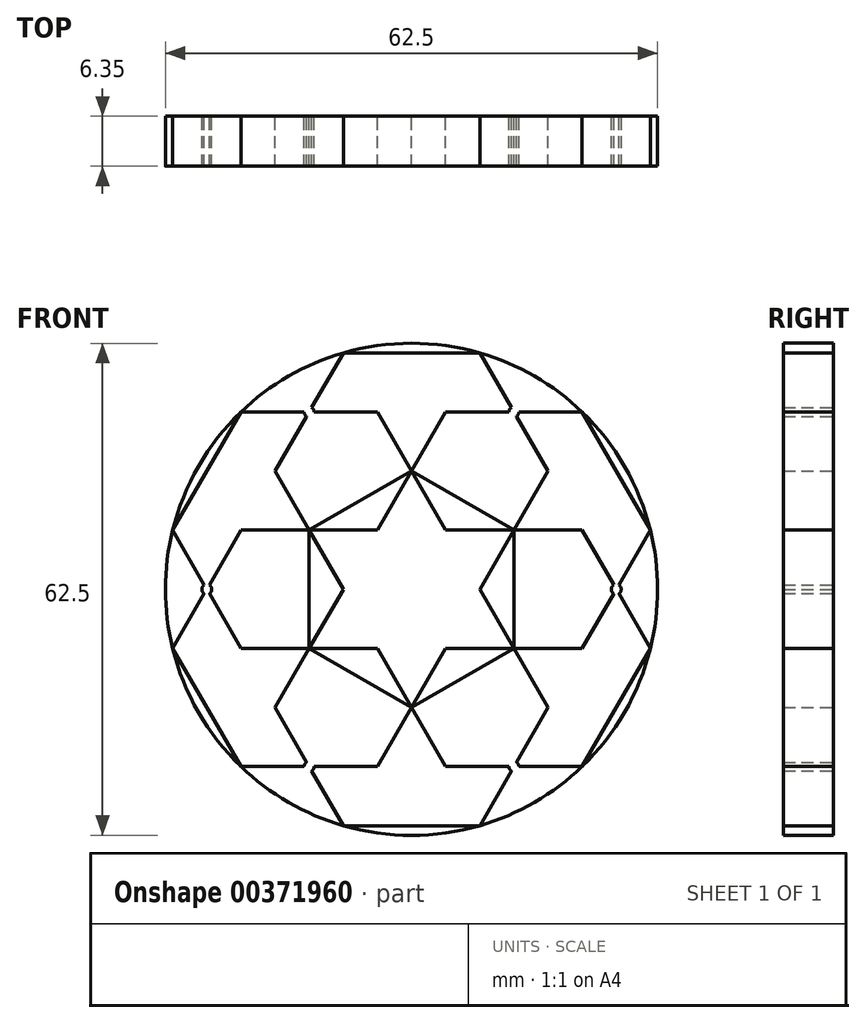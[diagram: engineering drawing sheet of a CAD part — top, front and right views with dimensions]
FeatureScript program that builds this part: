
annotation { "Feature Type Name" : "Feature", "Feature Type Description" : "" }
export const myFeature = defineFeature(function(context is Context, id is Id, definition is map)
    precondition{}
    {
        {
            var Q0;
            Q0=qCreatedBy(makeId("Front.planeOp"),FACE);
            var sketch = newSketch(context, id + "F0", { "sketchPlane" : qUnion([Q0])});
            skLineSegment(sketch, "E0.0", {"start": v(13, 7.5) * mm, "end": v(13, -7.5) * mm});
            skLineSegment(sketch, "E0.1", {"start": v(13, -7.5) * mm, "end": v(0, -15.01) * mm});
            skLineSegment(sketch, "E0.2", {"start": v(0, -15.01) * mm, "end": v(-13, -7.5) * mm});
            skLineSegment(sketch, "E0.3", {"start": v(-13, -7.5) * mm, "end": v(-13, 7.5) * mm});
            skLineSegment(sketch, "E0.4", {"start": v(-13, 7.5) * mm, "end": v(0, 15.01) * mm});
            skLineSegment(sketch, "E0.5", {"start": v(0, 15.01) * mm, "end": v(13, 7.5) * mm});
            skPoint(sketch, "E0.0.midPoint", {"position": v(13, 0) * mm});
            skLineSegment(sketch, "E1.0", {"start": v(17.34, 15.01) * mm, "end": v(8.67, 0) * mm});
            skLineSegment(sketch, "E1.1", {"start": v(8.67, 0) * mm, "end": v(-8.67, 0) * mm});
            skLineSegment(sketch, "E1.2", {"start": v(-8.67, 0) * mm, "end": v(-17.34, 15.01) * mm});
            skLineSegment(sketch, "E1.3", {"start": v(-17.34, 15.01) * mm, "end": v(-13.32, 21.97) * mm});
            skLineSegment(sketch, "E1.4", {"start": v(-8.67, 30.03) * mm, "end": v(8.67, 30.03) * mm});
            skLineSegment(sketch, "E1.5", {"start": v(8.67, 30.03) * mm, "end": v(12.69, 23.07) * mm});
            skPoint(sketch, "E1.0.midPoint", {"position": v(13, 7.5) * mm});
            skLineSegment(sketch, "E2.0", {"start": v(8.67, 0) * mm, "end": v(17.34, -15.01) * mm});
            skLineSegment(sketch, "E2.1", {"start": v(17.34, -15.01) * mm, "end": v(13.32, -21.97) * mm});
            skLineSegment(sketch, "E2.2", {"start": v(8.67, -30.03) * mm, "end": v(-8.67, -30.03) * mm});
            skLineSegment(sketch, "E2.3", {"start": v(-8.67, -30.03) * mm, "end": v(-12.69, -23.07) * mm});
            skLineSegment(sketch, "E2.4", {"start": v(-17.34, -15.01) * mm, "end": v(-8.67, 0) * mm});
            skLineSegment(sketch, "E2.5", {"start": v(-8.67, 0) * mm, "end": v(8.67, 0) * mm});
            skPoint(sketch, "E2.0.midPoint", {"position": v(13, -7.5) * mm});
            skLineSegment(sketch, "E3.0", {"start": v(4.33, 7.5) * mm, "end": v(21.67, 7.5) * mm});
            skLineSegment(sketch, "E3.1", {"start": v(21.67, 7.5) * mm, "end": v(25.69, 0.55) * mm});
            skLineSegment(sketch, "E3.2", {"start": v(30.34, -7.5) * mm, "end": v(21.67, -22.52) * mm});
            skLineSegment(sketch, "E3.3", {"start": v(21.67, -22.52) * mm, "end": v(13.64, -22.52) * mm});
            skLineSegment(sketch, "E3.4", {"start": v(4.33, -22.52) * mm, "end": v(-4.33, -7.5) * mm});
            skLineSegment(sketch, "E3.5", {"start": v(-4.33, -7.5) * mm, "end": v(4.33, 7.5) * mm});
            skLineSegment(sketch, "E4.0", {"start": v(-4.33, -7.5) * mm, "end": v(-21.67, -7.5) * mm});
            skLineSegment(sketch, "E4.1", {"start": v(-21.67, -7.5) * mm, "end": v(-25.69, -0.55) * mm});
            skLineSegment(sketch, "E4.2", {"start": v(-30.34, 7.5) * mm, "end": v(-21.67, 22.52) * mm});
            skLineSegment(sketch, "E4.3", {"start": v(-21.67, 22.52) * mm, "end": v(-13.64, 22.52) * mm});
            skLineSegment(sketch, "E4.4", {"start": v(-4.33, 22.52) * mm, "end": v(4.33, 7.5) * mm});
            skLineSegment(sketch, "E4.5", {"start": v(4.33, 7.5) * mm, "end": v(-4.33, -7.5) * mm});
            skPoint(sketch, "E4.0.midPoint", {"position": v(-13, -7.5) * mm});
            skLineSegment(sketch, "E5.0", {"start": v(4.33, -7.5) * mm, "end": v(-4.33, -22.52) * mm});
            skLineSegment(sketch, "E5.1", {"start": v(-4.33, -22.52) * mm, "end": v(-12.37, -22.52) * mm});
            skLineSegment(sketch, "E5.2", {"start": v(-21.67, -22.52) * mm, "end": v(-30.34, -7.5) * mm});
            skLineSegment(sketch, "E5.3", {"start": v(-30.34, -7.5) * mm, "end": v(-26.32, -0.55) * mm});
            skLineSegment(sketch, "E5.4", {"start": v(-21.67, 7.5) * mm, "end": v(-4.33, 7.5) * mm});
            skLineSegment(sketch, "E5.5", {"start": v(-4.33, 7.5) * mm, "end": v(4.33, -7.5) * mm});
            skPoint(sketch, "E5.0.midPoint", {"position": v(0, -15.01) * mm});
            skLineSegment(sketch, "E6.0", {"start": v(-4.33, 7.5) * mm, "end": v(4.33, 22.52) * mm});
            skLineSegment(sketch, "E6.1", {"start": v(4.33, 22.52) * mm, "end": v(12.37, 22.52) * mm});
            skLineSegment(sketch, "E6.2", {"start": v(21.67, 22.52) * mm, "end": v(30.34, 7.5) * mm});
            skLineSegment(sketch, "E6.3", {"start": v(30.34, 7.5) * mm, "end": v(26.32, 0.55) * mm});
            skLineSegment(sketch, "E6.4", {"start": v(21.67, -7.5) * mm, "end": v(4.33, -7.5) * mm});
            skLineSegment(sketch, "E6.5", {"start": v(4.33, -7.5) * mm, "end": v(-4.33, 7.5) * mm});
            skPoint(sketch, "E6.0.midPoint", {"position": v(0, 15.01) * mm});
            skPoint(sketch, "E0.cCircle.center.orphan", {"position": v(0, 0) * mm});
            skCircle(sketch, "E7", {"center": v(0, 0) * mm, "radius": 31.25 * mm});
            skCircle(sketch, "E8", {"center": v(-13, 22.52) * mm, "radius": 0.64 * mm});
            skCircle(sketch, "E9", {"center": v(13, 22.52) * mm, "radius": 0.64 * mm});
            skCircle(sketch, "E10", {"center": v(26, 0) * mm, "radius": 0.64 * mm});
            skCircle(sketch, "E11", {"center": v(13, -22.52) * mm, "radius": 0.64 * mm});
            skCircle(sketch, "E12", {"center": v(-13, -22.52) * mm, "radius": 0.64 * mm});
            skCircle(sketch, "E13", {"center": v(-26, 0) * mm, "radius": 0.64 * mm});
            skLineSegment(sketch, "E14.trimOffspring", {"start": v(-12.37, 22.52) * mm, "end": v(-4.33, 22.52) * mm});
            skLineSegment(sketch, "E15.trimOffspring", {"start": v(-12.69, 23.07) * mm, "end": v(-8.67, 30.03) * mm});
            skLineSegment(sketch, "E16.trimOffspring", {"start": v(13.64, 22.52) * mm, "end": v(21.67, 22.52) * mm});
            skLineSegment(sketch, "E17.trimOffspring", {"start": v(13.32, 21.97) * mm, "end": v(17.34, 15.01) * mm});
            skLineSegment(sketch, "E18.trimOffspring", {"start": v(26.32, -0.55) * mm, "end": v(30.34, -7.5) * mm});
            skLineSegment(sketch, "E19.trimOffspring", {"start": v(25.69, -0.55) * mm, "end": v(21.67, -7.5) * mm});
            skLineSegment(sketch, "E20.trimOffspring", {"start": v(12.69, -23.07) * mm, "end": v(8.67, -30.03) * mm});
            skLineSegment(sketch, "E21.trimOffspring", {"start": v(12.37, -22.52) * mm, "end": v(4.33, -22.52) * mm});
            skLineSegment(sketch, "E22.trimOffspring", {"start": v(-13.32, -21.97) * mm, "end": v(-17.34, -15.01) * mm});
            skLineSegment(sketch, "E23.trimOffspring", {"start": v(-13.64, -22.52) * mm, "end": v(-21.67, -22.52) * mm});
            skLineSegment(sketch, "E24.trimOffspring", {"start": v(-26.32, 0.55) * mm, "end": v(-30.34, 7.5) * mm});
            skLineSegment(sketch, "E25.trimOffspring", {"start": v(-25.69, 0.55) * mm, "end": v(-21.67, 7.5) * mm});
            skSolve(sketch);
        }
        {
            var Q0;
            {var subQ0=sQuery(id+"F0.wireOp",EDGE,"E1.4");Q0=makeQuery(id+"F0.imprint","IMPRINT",FACE,{"disambiguationData":[TD([[makeQuery(id+"F0.imprint","IMPRINT",EDGE,{"derivedFrom":subQ0}),1.0]])]});}
            var Q1;
            {var subQ0=sQuery(id+"F0.wireOp",EDGE,"E2.2");Q1=makeQuery(id+"F0.imprint","IMPRINT",FACE,{"disambiguationData":[TD([[makeQuery(id+"F0.imprint","IMPRINT",EDGE,{"derivedFrom":subQ0}),1.0]])]});}
            var Q2;
            {var subQ0=sQuery(id+"F0.wireOp",EDGE,"E3.2");Q2=makeQuery(id+"F0.imprint","IMPRINT",FACE,{"disambiguationData":[TD([[makeQuery(id+"F0.imprint","IMPRINT",EDGE,{"derivedFrom":subQ0}),1.0]])]});}
            var Q3;
            {var subQ0=sQuery(id+"F0.wireOp",EDGE,"E4.2");Q3=makeQuery(id+"F0.imprint","IMPRINT",FACE,{"disambiguationData":[TD([[makeQuery(id+"F0.imprint","IMPRINT",EDGE,{"derivedFrom":subQ0}),1.0]])]});}
            var Q4;
            {var subQ0=sQuery(id+"F0.wireOp",EDGE,"E5.2");Q4=makeQuery(id+"F0.imprint","IMPRINT",FACE,{"disambiguationData":[TD([[makeQuery(id+"F0.imprint","IMPRINT",EDGE,{"derivedFrom":subQ0}),1.0]])]});}
            var Q5;
            {var subQ0=sQuery(id+"F0.wireOp",EDGE,"E6.2");Q5=makeQuery(id+"F0.imprint","IMPRINT",FACE,{"disambiguationData":[TD([[makeQuery(id+"F0.imprint","IMPRINT",EDGE,{"derivedFrom":subQ0}),1.0]])]});}
            var Q6;
            {var subQ1=sQuery(id+"F0.wireOp",EDGE,"E1.5");var subQ3=sQuery(id+"F0.wireOp",EDGE,"E6.1");var subQ4=makeQuery(id+"F0.imprint","INTERSECT",VERTEX,{"derivedFrom":[subQ1,subQ3]});Q6=makeQuery(id+"F0.imprint","IMPRINT",FACE,{"disambiguationData":[TD([[makeQuery(id+"F0.imprint","IMPRINT",EDGE,{"disambiguationData":[TD([[subQ4,1.0]])],"derivedFrom":subQ1}),1.0]])]});}
            var Q7;
            {var subQ1=sQuery(id+"F0.wireOp",EDGE,"E2.3");var subQ3=sQuery(id+"F0.wireOp",EDGE,"E5.1");var subQ4=makeQuery(id+"F0.imprint","INTERSECT",VERTEX,{"derivedFrom":[subQ1,subQ3]});Q7=makeQuery(id+"F0.imprint","IMPRINT",FACE,{"disambiguationData":[TD([[makeQuery(id+"F0.imprint","IMPRINT",EDGE,{"disambiguationData":[TD([[subQ4,1.0]])],"derivedFrom":subQ1}),1.0]])]});}
            var Q8;
            {var subQ0=sQuery(id+"F0.wireOp",EDGE,"E3.5");var subQ1=sQuery(id+"F0.wireOp",EDGE,"E1.1");var subQ2=makeQuery(id+"F0.imprint","INTERSECT",VERTEX,{"derivedFrom":[subQ1,subQ0,sQuery(id+"F0.wireOp",EDGE,"E5.5")]});Q8=makeQuery(id+"F0.imprint","IMPRINT",FACE,{"disambiguationData":[TD([[makeQuery(id+"F0.imprint","IMPRINT",EDGE,{"disambiguationData":[TD([[subQ2,-1.0]])],"derivedFrom":subQ1}),1.0]])]});}
            var Q9;
            {var subQ3=sQuery(id+"F0.wireOp",EDGE,"E3.5");var subQ5=sQuery(id+"F0.wireOp",EDGE,"E5.5");var subQ6=makeQuery(id+"F0.imprint","INTERSECT",VERTEX,{"derivedFrom":[sQuery(id+"F0.wireOp",EDGE,"E1.1"),subQ3,subQ5]});Q9=makeQuery(id+"F0.imprint","IMPRINT",FACE,{"disambiguationData":[TD([[makeQuery(id+"F0.imprint","IMPRINT",EDGE,{"disambiguationData":[TD([[subQ6,1.0]])],"derivedFrom":subQ3}),-1.0]])]});}
            var Q10;
            {var subQ0=sQuery(id+"F0.wireOp",EDGE,"E5.5");var subQ1=sQuery(id+"F0.wireOp",EDGE,"E1.1");var subQ2=makeQuery(id+"F0.imprint","INTERSECT",VERTEX,{"derivedFrom":[subQ1,sQuery(id+"F0.wireOp",EDGE,"E3.5"),subQ0]});Q10=makeQuery(id+"F0.imprint","IMPRINT",FACE,{"disambiguationData":[TD([[makeQuery(id+"F0.imprint","IMPRINT",EDGE,{"disambiguationData":[TD([[subQ2,1.0]])],"derivedFrom":subQ1}),1.0]])]});}
            var Q11;
            {var subQ3=sQuery(id+"F0.wireOp",EDGE,"E1.1");var subQ5=sQuery(id+"F0.wireOp",EDGE,"E3.5");var subQ7=makeQuery(id+"F0.imprint","INTERSECT",VERTEX,{"derivedFrom":[subQ3,subQ5,sQuery(id+"F0.wireOp",EDGE,"E5.5")]});Q11=makeQuery(id+"F0.imprint","IMPRINT",FACE,{"disambiguationData":[TD([[makeQuery(id+"F0.imprint","IMPRINT",EDGE,{"disambiguationData":[TD([[subQ7,1.0]])],"derivedFrom":subQ3}),-1.0]])]});}
            var Q12;
            {var subQ0=sQuery(id+"F0.wireOp",EDGE,"E5.5");var subQ1=sQuery(id+"F0.wireOp",EDGE,"E3.5");var subQ2=makeQuery(id+"F0.imprint","INTERSECT",VERTEX,{"derivedFrom":[sQuery(id+"F0.wireOp",EDGE,"E1.1"),subQ1,subQ0]});Q12=makeQuery(id+"F0.imprint","IMPRINT",FACE,{"disambiguationData":[TD([[makeQuery(id+"F0.imprint","IMPRINT",EDGE,{"disambiguationData":[TD([[subQ2,-1.0]])],"derivedFrom":subQ1}),1.0]])]});}
            var Q13;
            {var subQ0=sQuery(id+"F0.wireOp",EDGE,"E5.5");var subQ1=sQuery(id+"F0.wireOp",EDGE,"E1.1");var subQ2=makeQuery(id+"F0.imprint","INTERSECT",VERTEX,{"derivedFrom":[subQ1,sQuery(id+"F0.wireOp",EDGE,"E3.5"),subQ0]});Q13=makeQuery(id+"F0.imprint","IMPRINT",FACE,{"disambiguationData":[TD([[makeQuery(id+"F0.imprint","IMPRINT",EDGE,{"disambiguationData":[TD([[subQ2,-1.0]])],"derivedFrom":subQ1}),-1.0]])]});}
            var Q14;
            {var subQ6=sQuery(id+"F0.wireOp",EDGE,"E0.4");Q14=makeQuery(id+"F0.imprint","IMPRINT",FACE,{"disambiguationData":[TD([[makeQuery(id+"F0.imprint","IMPRINT",EDGE,{"derivedFrom":subQ6}),1.0]])]});}
            var Q15;
            {var subQ1=sQuery(id+"F0.wireOp",EDGE,"E0.5");Q15=makeQuery(id+"F0.imprint","IMPRINT",FACE,{"disambiguationData":[TD([[makeQuery(id+"F0.imprint","IMPRINT",EDGE,{"derivedFrom":subQ1}),1.0]])]});}
            var Q16;
            {var subQ7=sQuery(id+"F0.wireOp",EDGE,"E0.0");Q16=makeQuery(id+"F0.imprint","IMPRINT",FACE,{"disambiguationData":[TD([[makeQuery(id+"F0.imprint","IMPRINT",EDGE,{"derivedFrom":subQ7}),1.0]])]});}
            var Q17;
            {var subQ7=sQuery(id+"F0.wireOp",EDGE,"E0.1");Q17=makeQuery(id+"F0.imprint","IMPRINT",FACE,{"disambiguationData":[TD([[makeQuery(id+"F0.imprint","IMPRINT",EDGE,{"derivedFrom":subQ7}),1.0]])]});}
            var Q18;
            {var subQ1=sQuery(id+"F0.wireOp",EDGE,"E0.2");Q18=makeQuery(id+"F0.imprint","IMPRINT",FACE,{"disambiguationData":[TD([[makeQuery(id+"F0.imprint","IMPRINT",EDGE,{"derivedFrom":subQ1}),1.0]])]});}
            var Q19;
            {var subQ7=sQuery(id+"F0.wireOp",EDGE,"E0.3");Q19=makeQuery(id+"F0.imprint","IMPRINT",FACE,{"disambiguationData":[TD([[makeQuery(id+"F0.imprint","IMPRINT",EDGE,{"derivedFrom":subQ7}),1.0]])]});}
            var Q20;
            {var subQ0=sQuery(id+"F0.wireOp",EDGE,"E4.3");Q20=makeQuery(id+"F0.imprint","IMPRINT",FACE,{"disambiguationData":[TD([[makeQuery(id+"F0.imprint","IMPRINT",EDGE,{"derivedFrom":subQ0}),1.0]])]});}
            var Q21;
            {var subQ0=sQuery(id+"F0.wireOp",EDGE,"E5.3");Q21=makeQuery(id+"F0.imprint","IMPRINT",FACE,{"disambiguationData":[TD([[makeQuery(id+"F0.imprint","IMPRINT",EDGE,{"derivedFrom":subQ0}),1.0]])]});}
            var Q22;
            {var subQ1=sQuery(id+"F0.wireOp",EDGE,"E6.3");Q22=makeQuery(id+"F0.imprint","IMPRINT",FACE,{"disambiguationData":[TD([[makeQuery(id+"F0.imprint","IMPRINT",EDGE,{"derivedFrom":subQ1}),1.0]])]});}
            var Q23;
            {var subQ0=sQuery(id+"F0.wireOp",EDGE,"E3.3");Q23=makeQuery(id+"F0.imprint","IMPRINT",FACE,{"disambiguationData":[TD([[makeQuery(id+"F0.imprint","IMPRINT",EDGE,{"derivedFrom":subQ0}),1.0]])]});}
            var Q24;
            {var subQ0=sQuery(id+"F0.wireOp",EDGE,"E11");var subQ1=makeQuery(id+"F0.imprint","INTERSECT",VERTEX,{"derivedFrom":[sQuery(id+"F0.wireOp",EDGE,"E2.1"),subQ0]});Q24=makeQuery(id+"F0.imprint","IMPRINT",FACE,{"disambiguationData":[TD([[makeQuery(id+"F0.imprint","IMPRINT",EDGE,{"disambiguationData":[TD([[subQ1,1.0]])],"derivedFrom":subQ0}),1.0]])]});}
            var Q25;
            {var subQ0=sQuery(id+"F0.wireOp",EDGE,"E12");var subQ1=makeQuery(id+"F0.imprint","INTERSECT",VERTEX,{"derivedFrom":[sQuery(id+"F0.wireOp",EDGE,"E2.3"),subQ0]});Q25=makeQuery(id+"F0.imprint","IMPRINT",FACE,{"disambiguationData":[TD([[makeQuery(id+"F0.imprint","IMPRINT",EDGE,{"disambiguationData":[TD([[subQ1,-1.0]])],"derivedFrom":subQ0}),1.0]])]});}
            var Q26;
            {var subQ0=sQuery(id+"F0.wireOp",EDGE,"E13");var subQ4=makeQuery(id+"F0.imprint","IMPRINT",VERTEX,{"derivedFrom":subQ0});Q26=makeQuery(id+"F0.imprint","IMPRINT",FACE,{"disambiguationData":[TD([[makeQuery(id+"F0.imprint","IMPRINT",EDGE,{"disambiguationData":[TD([[subQ4,1.0]])],"derivedFrom":subQ0}),1.0]])]});}
            var Q27;
            {var subQ0=sQuery(id+"F0.wireOp",EDGE,"E10");var subQ4=makeQuery(id+"F0.imprint","IMPRINT",VERTEX,{"derivedFrom":subQ0});Q27=makeQuery(id+"F0.imprint","IMPRINT",FACE,{"disambiguationData":[TD([[makeQuery(id+"F0.imprint","IMPRINT",EDGE,{"disambiguationData":[TD([[subQ4,1.0]])],"derivedFrom":subQ0}),1.0]])]});}
            var Q28;
            {var subQ0=sQuery(id+"F0.wireOp",EDGE,"E8");var subQ1=makeQuery(id+"F0.imprint","INTERSECT",VERTEX,{"derivedFrom":[subQ0,sQuery(id+"F0.wireOp",EDGE,"E14.trimOffspring")]});Q28=makeQuery(id+"F0.imprint","IMPRINT",FACE,{"disambiguationData":[TD([[makeQuery(id+"F0.imprint","IMPRINT",EDGE,{"disambiguationData":[TD([[subQ1,-1.0]])],"derivedFrom":subQ0}),1.0]])]});}
            var Q29;
            {var subQ0=sQuery(id+"F0.wireOp",EDGE,"E9");var subQ1=makeQuery(id+"F0.imprint","INTERSECT",VERTEX,{"derivedFrom":[subQ0,sQuery(id+"F0.wireOp",EDGE,"E16.trimOffspring")]});Q29=makeQuery(id+"F0.imprint","IMPRINT",FACE,{"disambiguationData":[TD([[makeQuery(id+"F0.imprint","IMPRINT",EDGE,{"disambiguationData":[TD([[subQ1,1.0]])],"derivedFrom":subQ0}),1.0]])]});}
            extrude(context, id + "F1", {"entities" : qUnion([Q0, Q1, Q2, Q3, Q4, Q5, Q6, Q7, Q8, Q9, Q10, Q11, Q12, Q13, Q14, Q15, Q16, Q17, Q18, Q19, Q20, Q21, Q22, Q23, Q24, Q25, Q26, Q27, Q28, Q29]), "depth" : 6.35 * mm, "offsetDistance" : 25.4 * mm});
        }
    });
